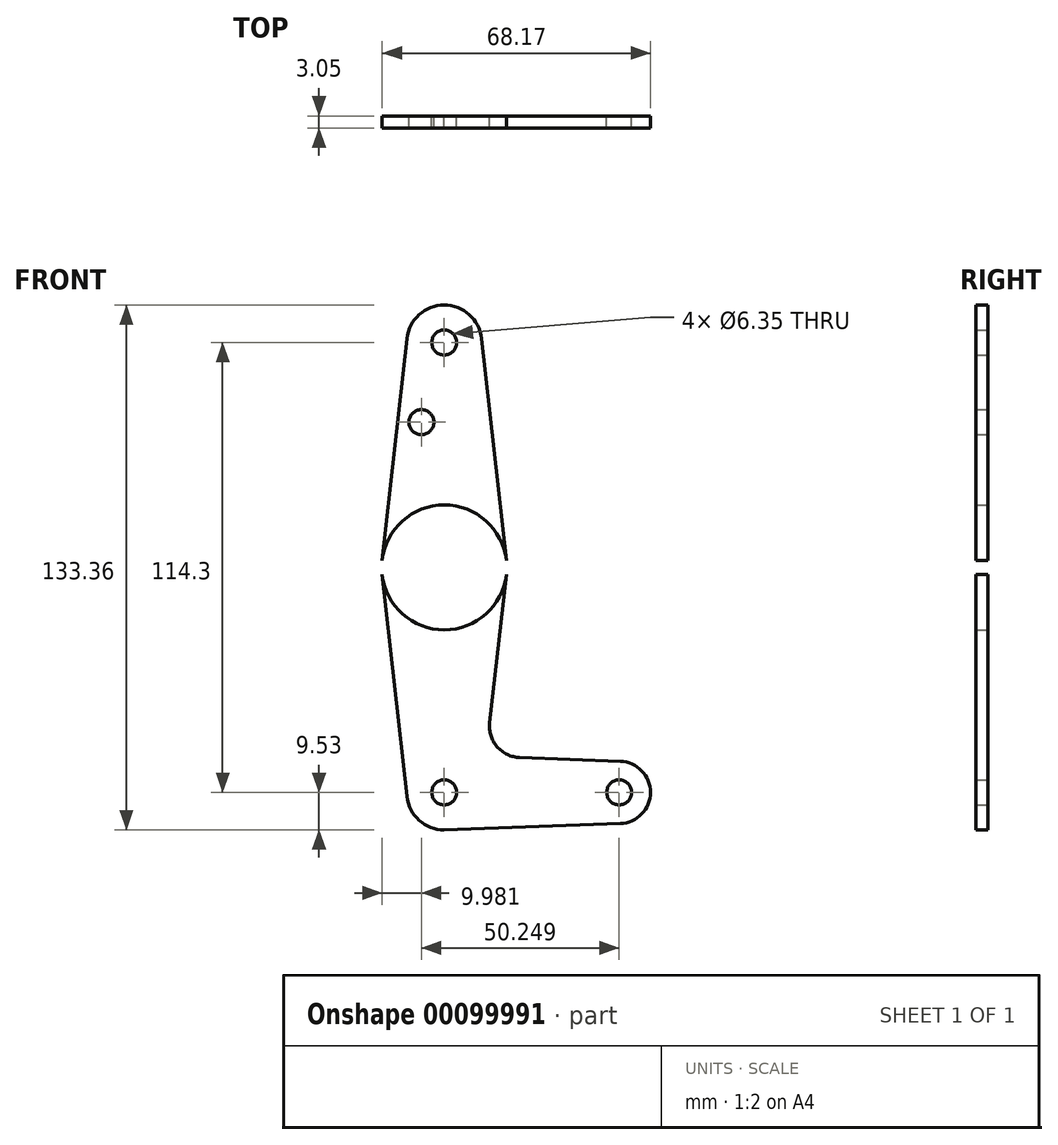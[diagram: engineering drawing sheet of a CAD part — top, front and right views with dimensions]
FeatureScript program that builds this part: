
annotation { "Feature Type Name" : "Feature", "Feature Type Description" : "" }
export const myFeature = defineFeature(function(context is Context, id is Id, definition is map)
    precondition{}
    {
        {
            var Q0;
            Q0=qCreatedBy(makeId("Front.planeOp"),FACE);
            var sketch = newSketch(context, id + "F0", { "sketchPlane" : qUnion([Q0])});
            skLineSegment(sketch, "E0", {"start": v(0, 114.3) * mm, "end": v(0, 0) * mm});
            skLineSegment(sketch, "E1", {"start": v(0, 0) * mm, "end": v(44.45, 0) * mm});
            skCircle(sketch, "E2", {"center": v(0, 114.3) * mm, "radius": 9.53 * mm});
            skCircle(sketch, "E3", {"center": v(0, 57.15) * mm, "radius": 15.88 * mm});
            skCircle(sketch, "E4", {"center": v(0, 0) * mm, "radius": 9.53 * mm});
            skCircle(sketch, "E5", {"center": v(44.45, 0) * mm, "radius": 7.94 * mm});
            skLineSegment(sketch, "E6", {"start": v(-9.47, 115.36) * mm, "end": v(-15.78, 58.91) * mm});
            skLineSegment(sketch, "E7", {"start": v(9.47, 115.36) * mm, "end": v(15.78, 58.91) * mm});
            skLineSegment(sketch, "E8", {"start": v(15.78, 55.39) * mm, "end": v(11.56, 17.67) * mm});
            skLineSegment(sketch, "E9", {"start": v(19.18, 8.85) * mm, "end": v(44.73, 7.93) * mm});
            skLineSegment(sketch, "E10", {"start": v(0, -9.53) * mm, "end": v(44.73, -7.93) * mm});
            skLineSegment(sketch, "E11", {"start": v(-15.78, 55.39) * mm, "end": v(-9.47, -1.06) * mm});
            skCircle(sketch, "E12", {"center": v(-5.8, 94.06) * mm, "radius": 3.18 * mm});
            skCircle(sketch, "E13", {"center": v(0, 57.15) * mm, "radius": 3.18 * mm});
            skCircle(sketch, "E14", {"center": v(0, 114.3) * mm, "radius": 3.18 * mm});
            skCircle(sketch, "E15", {"center": v(0, 0) * mm, "radius": 3.18 * mm});
            skCircle(sketch, "E16", {"center": v(44.45, 0) * mm, "radius": 3.18 * mm});
            skArc(sketch, "E17.filletArc", {"start": v(11.56, 17.67) * mm, "mid": v(13.44, 11.6) * mm, "end": v(19.18, 8.85) * mm});
            skSolve(sketch);
        }
        {
            var Q0;
            {var subQ5=sQuery(id+"F0.wireOp",EDGE,"E7");Q0=makeQuery(id+"F0.imprint","IMPRINT",FACE,{"disambiguationData":[TD([[makeQuery(id+"F0.imprint","IMPRINT",EDGE,{"derivedFrom":subQ5}),-1.0]])]});}
            var Q1;
            {var subQ0=sQuery(id+"F0.wireOp",EDGE,"E6");Q1=makeQuery(id+"F0.imprint","IMPRINT",FACE,{"disambiguationData":[TD([[makeQuery(id+"F0.imprint","IMPRINT",EDGE,{"derivedFrom":subQ0}),1.0]])]});}
            var Q2;
            Q2=makeQuery(id+"F0.imprint","IMPRINT",FACE,{"disambiguationData":[TD([[makeQuery(id+"F0.imprint","IMPRINT",EDGE,{"derivedFrom":sQuery(id+"F0.wireOp",EDGE,"E14")}),-1.0]])]});
            var Q3;
            {var subQ0=sQuery(id+"F0.wireOp",EDGE,"E3");var subQ2=sQuery(id+"F0.wireOp",EDGE,"E0");var subQ3=makeQuery(id+"F0.imprint","INTERSECT",VERTEX,{"disambiguationData":[OD(0.0)],"derivedFrom":[subQ2,subQ0]});Q3=makeQuery(id+"F0.imprint","IMPRINT",FACE,{"disambiguationData":[TD([[makeQuery(id+"F0.imprint","IMPRINT",EDGE,{"disambiguationData":[TD([[subQ3,-1.0]])],"derivedFrom":subQ2}),1.0]])]});}
            var Q4;
            {var subQ0=sQuery(id+"F0.wireOp",EDGE,"E3");var subQ3=sQuery(id+"F0.wireOp",EDGE,"E0");var subQ4=makeQuery(id+"F0.imprint","INTERSECT",VERTEX,{"disambiguationData":[OD(0.0)],"derivedFrom":[subQ3,subQ0]});Q4=makeQuery(id+"F0.imprint","IMPRINT",FACE,{"disambiguationData":[TD([[makeQuery(id+"F0.imprint","IMPRINT",EDGE,{"disambiguationData":[TD([[subQ4,-1.0]])],"derivedFrom":subQ3}),-1.0]])]});}
            var Q5;
            {var subQ5=sQuery(id+"F0.wireOp",EDGE,"E11");Q5=makeQuery(id+"F0.imprint","IMPRINT",FACE,{"disambiguationData":[TD([[makeQuery(id+"F0.imprint","IMPRINT",EDGE,{"derivedFrom":subQ5}),1.0]])]});}
            var Q6;
            {var subQ0=sQuery(id+"F0.wireOp",EDGE,"E8");Q6=makeQuery(id+"F0.imprint","IMPRINT",FACE,{"disambiguationData":[TD([[makeQuery(id+"F0.imprint","IMPRINT",EDGE,{"derivedFrom":subQ0}),-1.0]])]});}
            var Q7;
            {var subQ0=sQuery(id+"F0.wireOp",EDGE,"E5");var subQ1=sQuery(id+"F0.wireOp",EDGE,"E1");var subQ2=makeQuery(id+"F0.imprint","INTERSECT",VERTEX,{"derivedFrom":[subQ1,subQ0]});Q7=makeQuery(id+"F0.imprint","IMPRINT",FACE,{"disambiguationData":[TD([[makeQuery(id+"F0.imprint","IMPRINT",EDGE,{"disambiguationData":[TD([[subQ2,1.0]])],"derivedFrom":subQ1}),-1.0]])]});}
            var Q8;
            {var subQ0=sQuery(id+"F0.wireOp",EDGE,"E4");var subQ1=sQuery(id+"F0.wireOp",EDGE,"E0");var subQ2=makeQuery(id+"F0.imprint","INTERSECT",VERTEX,{"derivedFrom":[subQ1,subQ0]});Q8=makeQuery(id+"F0.imprint","IMPRINT",FACE,{"disambiguationData":[TD([[makeQuery(id+"F0.imprint","IMPRINT",EDGE,{"disambiguationData":[TD([[subQ2,-1.0]])],"derivedFrom":subQ1}),1.0]])]});}
            var Q9;
            Q9=makeQuery(id+"F0.imprint","IMPRINT",FACE,{"disambiguationData":[TD([[makeQuery(id+"F0.imprint","IMPRINT",EDGE,{"derivedFrom":sQuery(id+"F0.wireOp",EDGE,"E16")}),-1.0]])]});
            var Q10;
            {var subQ3=sQuery(id+"F0.wireOp",EDGE,"E4");var subQ8=sQuery(id+"F0.wireOp",EDGE,"E0");var subQ9=makeQuery(id+"F0.imprint","INTERSECT",VERTEX,{"derivedFrom":[subQ8,subQ3]});Q10=makeQuery(id+"F0.imprint","IMPRINT",FACE,{"disambiguationData":[TD([[makeQuery(id+"F0.imprint","IMPRINT",EDGE,{"disambiguationData":[TD([[subQ9,-1.0]])],"derivedFrom":subQ8}),-1.0]])]});}
            extrude(context, id + "F1", {"entities" : qUnion([Q0, Q1, Q2, Q3, Q4, Q5, Q6, Q7, Q8, Q9, Q10]), "depth" : 3.05 * mm});
        }
    });
